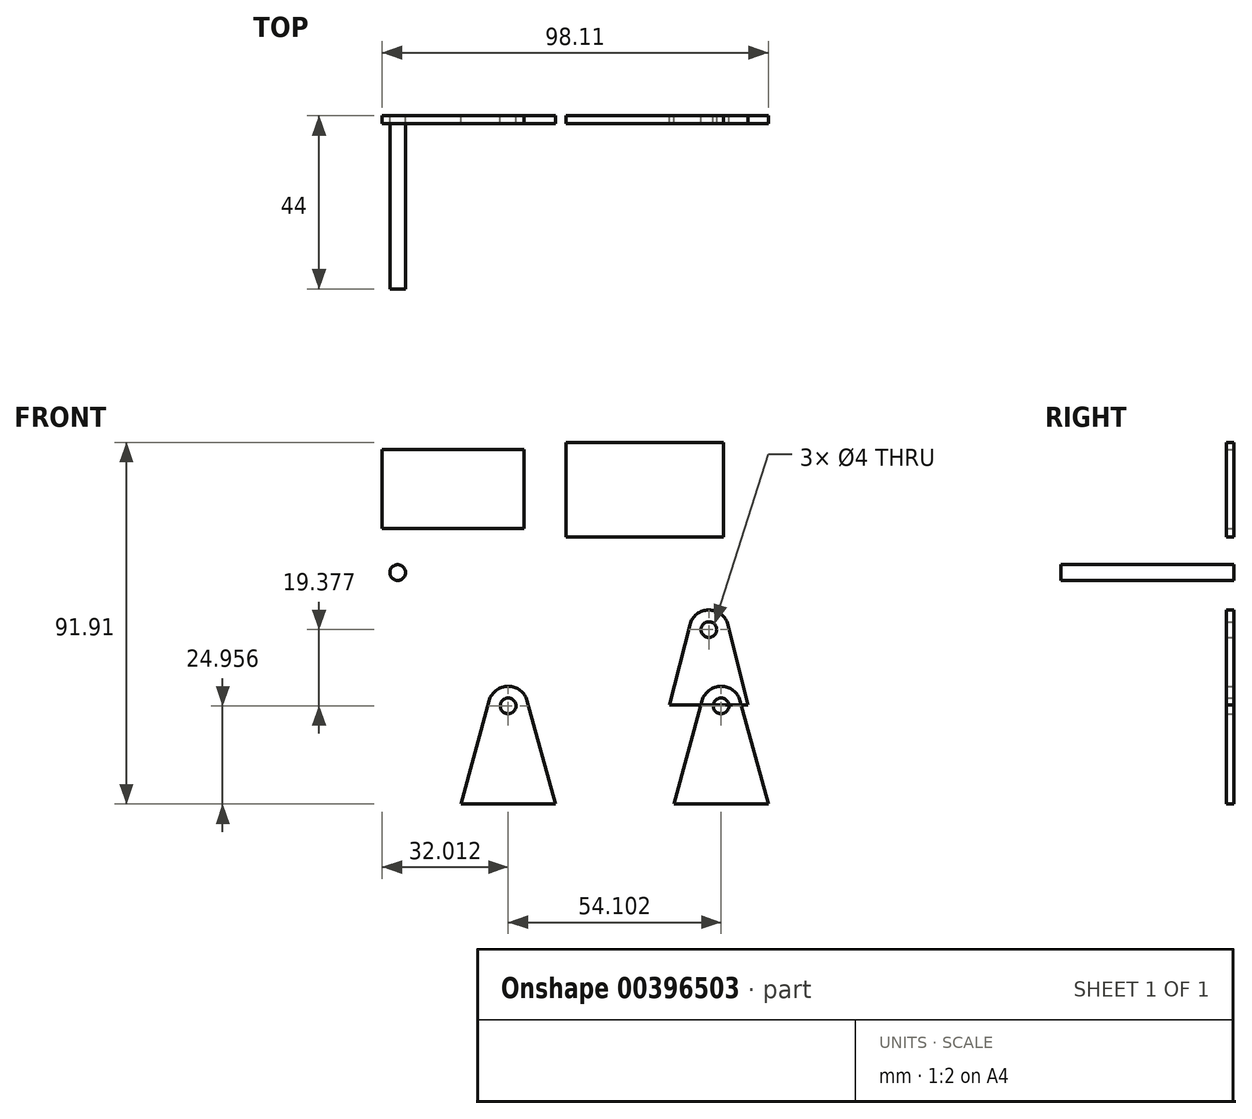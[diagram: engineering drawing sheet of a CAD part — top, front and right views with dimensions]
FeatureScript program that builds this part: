
annotation { "Feature Type Name" : "Feature", "Feature Type Description" : "" }
export const myFeature = defineFeature(function(context is Context, id is Id, definition is map)
    precondition{}
    {
        {
            var Q0;
            Q0=qCreatedBy(makeId("Front.planeOp"),FACE);
            var sketch = newSketch(context, id + "F0", { "sketchPlane" : qUnion([Q0])});
            skLineSegment(sketch, "E0.bottom", {"start": v(-22.6, 5.8) * mm, "end": v(17.4, 5.8) * mm});
            skLineSegment(sketch, "E0.top", {"start": v(-22.6, -18.2) * mm, "end": v(17.4, -18.2) * mm});
            skLineSegment(sketch, "E0.left", {"start": v(-22.6, 5.8) * mm, "end": v(-22.6, -18.2) * mm});
            skLineSegment(sketch, "E0.right", {"start": v(17.4, 5.8) * mm, "end": v(17.4, -18.2) * mm});
            skSolve(sketch);
        }
        {
            var Q0;
            Q0 = qSketchRegion(id + "F0", true);
            extrude(context, id + "F1", {"entities" : qUnion([Q0]), "depth" : 2 * mm});
        }
        {
            var Q0;
            Q0=qCreatedBy(makeId("Front.planeOp"),FACE);
            var sketch = newSketch(context, id + "F2", { "sketchPlane" : qUnion([Q0])});
            skLineSegment(sketch, "E1.top", {"start": v(-49.35, -86.11) * mm, "end": v(-25.35, -86.11) * mm});
            skCircle(sketch, "E2", {"center": v(-37.35, -61.15) * mm, "radius": 2 * mm});
            skCircle(sketch, "E3", {"center": v(-37.35, -61.15) * mm, "radius": 5 * mm});
            skLineSegment(sketch, "E4", {"start": v(-49.35, -86.11) * mm, "end": v(-42.17, -59.84) * mm});
            skLineSegment(sketch, "E5", {"start": v(-25.35, -86.11) * mm, "end": v(-32.52, -59.84) * mm});
            skSolve(sketch);
        }
        {
            var Q0;
            Q0 = qSketchRegion(id + "F2", true);
            extrude(context, id + "F3", {"entities" : qUnion([Q0]), "depth" : 2 * mm});
        }
        {
            var Q0;
            Q0=qCreatedBy(makeId("Front.planeOp"),FACE);
            var sketch = newSketch(context, id + "F4", { "sketchPlane" : qUnion([Q0])});
            skCircle(sketch, "E6", {"center": v(-65.4, -27.28) * mm, "radius": 2 * mm});
            skSolve(sketch);
        }
        {
            var Q0;
            Q0 = qSketchRegion(id + "F4", true);
            extrude(context, id + "F5", {"entities" : qUnion([Q0]), "depth" : 44 * mm});
        }
        {
            var Q0;
            Q0=qCreatedBy(makeId("Front.planeOp"),FACE);
            var sketch = newSketch(context, id + "F6", { "sketchPlane" : qUnion([Q0])});
            skLineSegment(sketch, "E7.bottom", {"start": v(-69.36, 3.94) * mm, "end": v(-33.36, 3.94) * mm});
            skLineSegment(sketch, "E7.top", {"start": v(-69.36, -16.06) * mm, "end": v(-33.36, -16.06) * mm});
            skLineSegment(sketch, "E7.left", {"start": v(-69.36, 3.94) * mm, "end": v(-69.36, -16.06) * mm});
            skLineSegment(sketch, "E7.right", {"start": v(-33.36, 3.94) * mm, "end": v(-33.36, -16.06) * mm});
            skSolve(sketch);
        }
        {
            var Q0;
            Q0 = qSketchRegion(id + "F6", true);
            extrude(context, id + "F7", {"entities" : qUnion([Q0]), "depth" : 2 * mm});
        }
        {
            var Q0;
            Q0=qCreatedBy(makeId("Front.planeOp"),FACE);
            var sketch = newSketch(context, id + "F8", { "sketchPlane" : qUnion([Q0])});
            skLineSegment(sketch, "E8.top", {"start": v(3.65, -60.9) * mm, "end": v(23.65, -60.9) * mm});
            skCircle(sketch, "E9", {"center": v(13.65, -41.78) * mm, "radius": 2 * mm});
            skCircle(sketch, "E10", {"center": v(13.65, -41.78) * mm, "radius": 5 * mm});
            skLineSegment(sketch, "E11", {"start": v(3.65, -60.9) * mm, "end": v(8.8, -40.55) * mm});
            skLineSegment(sketch, "E12", {"start": v(23.65, -60.9) * mm, "end": v(18.5, -40.55) * mm});
            skSolve(sketch);
        }
        {
            var Q0;
            Q0 = qSketchRegion(id + "F8", true);
            extrude(context, id + "F9", {"entities" : qUnion([Q0]), "depth" : 2 * mm});
        }
        {
            var Q0;
            Q0=makeQuery(id+"F3.opExtrude","SWEPT_BODY",BODY,{"disambiguationData":[OSD([sQuery(id+"F2.wireOp",EDGE,"E1.top"),sQuery(id+"F2.wireOp",EDGE,"E2"),sQuery(id+"F2.wireOp",EDGE,"E3"),sQuery(id+"F2.wireOp",EDGE,"E4"),sQuery(id+"F2.wireOp",EDGE,"E5")])]});
            transform(context, id + "F10", {"entities" : qUnion([Q0]), "transformType" : TransformType.TRANSLATION_3D, "dx" : 54.1 * mm, "dy" : 0 * mm, "dz" : 0 * mm, "makeCopy" : true});
        }
    });
